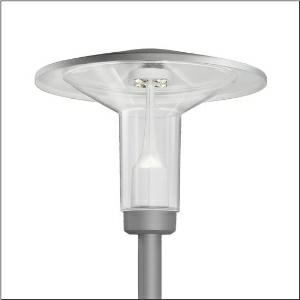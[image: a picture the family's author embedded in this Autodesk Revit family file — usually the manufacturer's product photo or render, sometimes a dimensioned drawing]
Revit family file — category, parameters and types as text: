
# Revit family: laterne_iq___st1_2a_5xa5255ef14hp_6738
name_source: partatom
category: Lighting Fixtures
units: mm (PartAtom-declared; Revit-internal decimal feet)

## family parameters
Cut with Voids When Loaded = No
Host = Face
Light Source = No
Part Type = Normal
Room Calculation Point = No
Round Connector Dimension = Use Diameter
Shared = No

## types (1)
- --- (1 x LED, 4730 lm, 33.6 W, 3000K)
    Apparent Load = 34 VA
    CIE Flux Codes = 25 63 94 98 100
    Color Rendering = 70
    Color Temperature = 3000K
    Default Elevation = 1800 mm
    Description = Lantern iQ, mast luminaire, Module 540 iQ-SR, primary light control with 3 zone facetted reflector, of plastic, silver coated, highly specular, structured, primary optical cover: cover, of PMMA, transparent, light distribution: ST1.2a, light emission: direct distribution, primary light characteristic: asymmetric, installation type: post-top, LED, High Power LED, rated luminous flux: 4.730lm, luminous efficacy: 141lm/W, light colour: 730, colour temperature: 3000K, control gear: iQ Street-Remote, control: pre-setting: logarithmic dimming characteristic, Street-Remote, Auto-Match, Temp-Guard, Lumen-Switch, Night-Set, Smart-Wire, Light-Fading, Desk-Remote (wireless, voltage-free reading and setting of iQ features in the workshop via application-optimized NFC function/RFID function), optimised constant luminous flux control (CLO 2.0), with terminal, 6-pole, max. 2.5mm², mains connection: 230..240V, AC, 50/60Hz, start of lifetime: 34W, end of service life: 36W, reduction: 15W, luminaire housing, upper part, of glass-fibre reinforced polyester, coated, Siteco® metallic grey (DB 702S), diameter: 750mm, height: 583mm, spigot size: d x l = 76 x 70mm (post-top) | with reducer (optional accessory) 60 x 70mm, mounting height: 3..5m, post-top mast mounting element, of diecast aluminium, coated, Siteco® metallic grey (DB 702S), Module 540 iQ-SR, traffic white (RAL 9016), equipment: Power, protection rating (complete): IP65, insulation class (complete): insulation class II (safety insulation), certification: CE, ENEC, VDE, packaging unit: 1 piece

Light Distribution: ST1.2a
    Height = 583 mm
    Lamp = 1 x LED
    Lamp Light Flux = 4730 lm
    Lamp Power = 33.6 W
    Lamp count = 1
    Length = 750 mm
    Luminous efficacy = 141 lm/W
    Manufacturer = Siteco
    ModVariant = No
    Model = 5XA5255EF14HP
    Number of Poles = 1
    OnlyDefault = Yes
    Power Factor = 1
    Product Name = Laterne iQ | ST1.2a
    Product group = mast luminaire | pylon top
    ProductGroupID = 6100
    Protection Class = Protection class II
    Protection Degree = IP 65
    RLX_Detail_Level = 1
    RLX_Emergency_Light_Flux = 0 lm
    RLX_Emergency_Type = 0
    RLX_Emergency_Type_DB = No
    RlxData = <blob elided: 34269 chars, md5=f281d71b>
    Socket = socket
    Standby Power = 0 W
    System Light Flux = 4730 lm
    System Power = 34 W
    Type Comments = factory setting: luminous flux: 100 % | dim-lin: 254 | 695 mA
    Type Image = l_1006050.jpg
    URL = http://relux.com
    VarID = @adj_214807
    Voltage = 0 V
    Weight = 0.00 kg
    Width = 0 mm  [stored 0 ft]

note: [stored X ft] marks values corroborated as IEEE doubles in the binary element streams (Revit-internal decimal feet)

## geometry (parser evidence)
native form markers: Blend x4, Sweep x9
no freeform markers — native parametric forms only
